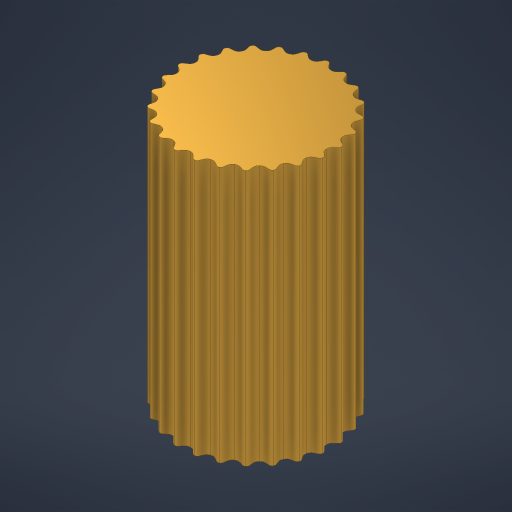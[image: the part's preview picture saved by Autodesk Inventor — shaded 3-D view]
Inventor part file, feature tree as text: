
AUTODESK INVENTOR PART (.ipt)
format: ipt  version: 2023.2 (Build 272271000, 271)  size: 420,352 bytes
history: native  units: mm
features: extrude x1, sketch x1
ambient origin geometry x8: Origin, YZ Plane, XZ Plane, XY Plane, X Axis, Y Axis, Z Axis, Center Point
bodies: Volumenkörper1 (feature_tree)
feature tree (2):
  extrude  "Extrusion1"  Depth=5.5mm
  sketch  "Skizze1"  dims[d0=6.0mm d1=5.5mm d2=500.0mm d4=360.0deg d8=10.0mm d9=15.0mm d10=250.0mm d12=360.0deg d14=10.0mm d15=0.0mm]
